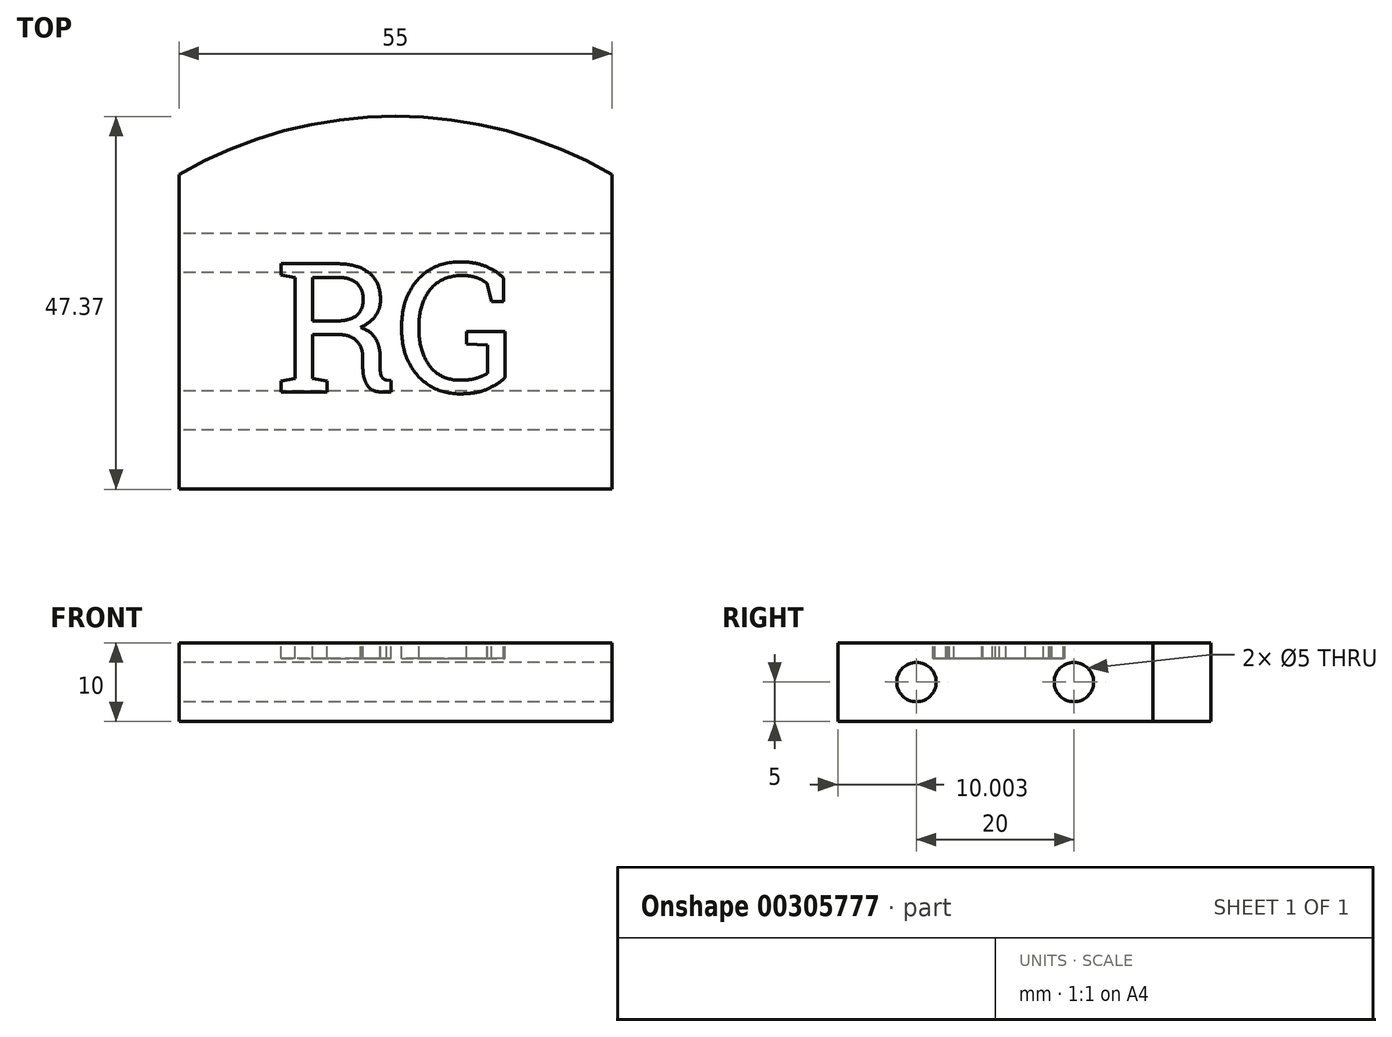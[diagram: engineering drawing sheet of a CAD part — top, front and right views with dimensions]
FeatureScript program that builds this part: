
annotation { "Feature Type Name" : "Feature", "Feature Type Description" : "" }
export const myFeature = defineFeature(function(context is Context, id is Id, definition is map)
    precondition{}
    {
        {
            var Q0;
            Q0=qCreatedBy(makeId("Top.planeOp"),FACE);
            var sketch = newSketch(context, id + "F0", { "sketchPlane" : qUnion([Q0])});
            skLineSegment(sketch, "E0.bottom", {"start": v(-36.1, 20.3) * mm, "end": v(18.9, 20.3) * mm});
            skLineSegment(sketch, "E0.top", {"start": v(-36.1, -19.7) * mm, "end": v(18.9, -19.7) * mm});
            skLineSegment(sketch, "E0.left", {"start": v(-36.1, 20.3) * mm, "end": v(-36.1, -19.7) * mm});
            skLineSegment(sketch, "E0.right", {"start": v(18.9, 20.3) * mm, "end": v(18.9, -19.7) * mm});
            skArc(sketch, "E1", {"start": v(18.9, 20.3) * mm, "mid": v(-8.6, 27.66) * mm, "end": v(-36.1, 20.3) * mm});
            skSolve(sketch);
        }
        {
            var Q0;
            Q0 = qSketchRegion(id + "F0", true);
            extrude(context, id + "F1", {"entities" : qUnion([Q0]), "depth" : 10 * mm});
        }
        {
            var Q0;
            Q0=makeQuery(id+"F1.opExtrude","SWEPT_FACE",FACE,{"disambiguationData":[OSD([sQuery(id+"F0.wireOp",EDGE,"E0.left")])]});
            var sketch = newSketch(context, id + "F2", { "sketchPlane" : qUnion([Q0])});
            skLineSegment(sketch, "E2", {"start": v(19.7, 5) * mm, "end": v(-20.3, 5) * mm, "construction": true});
            skCircle(sketch, "E3", {"center": v(9.7, 5) * mm, "radius": 2.5 * mm});
            skCircle(sketch, "E4", {"center": v(-10.3, 5) * mm, "radius": 2.5 * mm});
            skSolve(sketch);
        }
        {
            var Q0;
            Q0 = qSketchRegion(id + "F2", true);
            extrude(context, id + "F3", {"entities" : qUnion([Q0]), "operationType" : NewBodyOperationType.REMOVE, "endBound" : BoundingType.UP_TO_NEXT, "oppositeDirection" : true, "depth" : 25 * mm});
        }
        {
            var Q0;
            Q0=makeQuery(id+"F1.opExtrude","CAP_FACE",FACE,{"disambiguationData":[OSD([sQuery(id+"F0.wireOp",EDGE,"E0.top"),sQuery(id+"F0.wireOp",EDGE,"E0.left"),sQuery(id+"F0.wireOp",EDGE,"E0.right"),sQuery(id+"F0.wireOp",EDGE,"E1")])],"isStart":false});
            var sketch = newSketch(context, id + "F4", { "sketchPlane" : qUnion([Q0])});
            skText(sketch, "E5", { "text": "RG", "fontName": "RobotoSlab-Regular.ttf"});
            skLineSegment(sketch, "E6", {"start": v(-36.1, 0.3) * mm, "end": v(18.9, 0) * mm, "construction": true});
            skPoint(sketch, "E6.endSnap0", {"position": v(18.9, 0.3) * mm});
            skLineSegment(sketch, "E7", {"start": v(-8.6, 27.66) * mm, "end": v(-8.6, -19.7) * mm, "construction": true});
            const initialGuessF4  = {"E5": [-0.02395, -0.00735, 1, 0, 0.0165]};
            skSetInitialGuess(sketch, initialGuessF4);
            skSolve(sketch);
        }
        {
            var Q0;
            Q0 = qSketchRegion(id + "F4", true);
            extrude(context, id + "F5", {"entities" : qUnion([Q0]), "operationType" : NewBodyOperationType.REMOVE, "oppositeDirection" : true, "depth" : 2 * mm});
        }
    });
